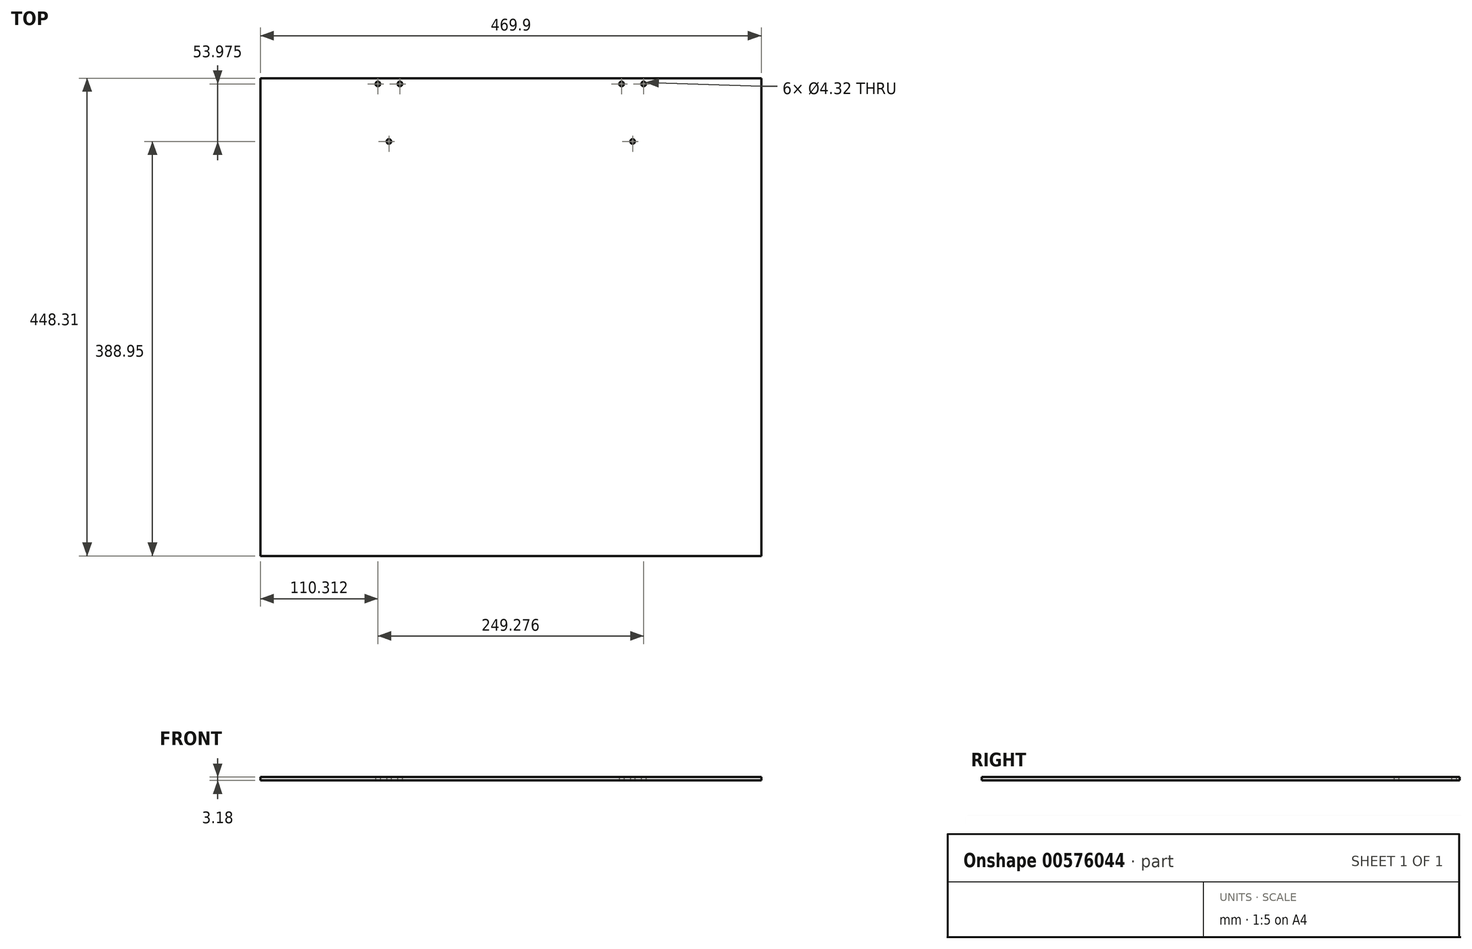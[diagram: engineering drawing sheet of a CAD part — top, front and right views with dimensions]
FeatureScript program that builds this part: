
annotation { "Feature Type Name" : "Feature", "Feature Type Description" : "" }
export const myFeature = defineFeature(function(context is Context, id is Id, definition is map)
    precondition{}
    {
        {
            var Q0;
            Q0=qCreatedBy(makeId("Top.planeOp"),FACE);
            var sketch = newSketch(context, id + "F0", { "sketchPlane" : qUnion([Q0])});
            skLineSegment(sketch, "E0.bottom", {"start": v(234.95, -234.95) * mm, "end": v(-234.95, -234.95) * mm});
            skLineSegment(sketch, "E0.top", {"start": v(234.95, 234.95) * mm, "end": v(-234.95, 234.95) * mm});
            skLineSegment(sketch, "E0.left", {"start": v(234.95, -234.95) * mm, "end": v(234.95, 234.95) * mm});
            skLineSegment(sketch, "E0.right", {"start": v(-234.95, -234.95) * mm, "end": v(-234.95, 234.95) * mm});
            skPoint(sketch, "E0.middle", {"position": v(0, 0) * mm});
            skSolve(sketch);
        }
        {
            var Q0;
            Q0=qSketchRegion(id+"F0",true);
            extrude(context, id + "F1", {"entities" : qUnion([Q0]), "depth" : 3.17 * mm, "offsetDistance" : 25.4 * mm});
        }
        {
            var Q0;
            Q0=makeQuery(id+"F1.opExtrude","CAP_FACE",FACE,{"disambiguationData":[OSD([sQuery(id+"F0.wireOp",EDGE,"E0.bottom"),sQuery(id+"F0.wireOp",EDGE,"E0.top"),sQuery(id+"F0.wireOp",EDGE,"E0.left"),sQuery(id+"F0.wireOp",EDGE,"E0.right")])],"isStart":true});
            var sketch = newSketch(context, id + "F2", { "sketchPlane" : qUnion([Q0])});
            skLineSegment(sketch, "E1", {"start": v(234.95, -234.95) * mm, "end": v(158.75, -234.95) * mm});
            skLineSegment(sketch, "E2", {"start": v(158.75, -234.95) * mm, "end": v(114.3, -234.95) * mm});
            skLineSegment(sketch, "E3", {"start": v(114.3, -234.95) * mm, "end": v(114.3, -214.33) * mm});
            skLineSegment(sketch, "E4", {"start": v(114.3, -214.33) * mm, "end": v(124.64, -214.33) * mm});
            skLineSegment(sketch, "E5", {"start": v(114.3, -234.95) * mm, "end": v(114.3, -160.35) * mm});
            skLineSegment(sketch, "E6.MirrorCS", {"start": v(114.3, -214.33) * mm, "end": v(103.96, -214.33) * mm});
            skLineSegment(sketch, "E7", {"start": v(0, -234.95) * mm, "end": v(0, -342.5) * mm});
            skLineSegment(sketch, "E8.MirrorCS", {"start": v(-158.75, -234.95) * mm, "end": v(-114.3, -234.95) * mm});
            skLineSegment(sketch, "E9.MirrorCS", {"start": v(-114.3, -214.33) * mm, "end": v(-124.64, -214.33) * mm});
            skLineSegment(sketch, "E10.MirrorCS", {"start": v(-114.3, -214.33) * mm, "end": v(-103.96, -214.33) * mm});
            skLineSegment(sketch, "E11.MirrorCS", {"start": v(-234.95, -234.95) * mm, "end": v(-158.75, -234.95) * mm});
            skLineSegment(sketch, "E12.MirrorCS", {"start": v(-114.3, -234.95) * mm, "end": v(-114.3, -214.33) * mm});
            skLineSegment(sketch, "E13.MirrorCS", {"start": v(-114.3, -234.95) * mm, "end": v(-114.3, -160.35) * mm});
            skSolve(sketch);
        }
        {
            var Q0;
            Q0=sQuery(id+"F2.wireOp",VERTEX,"E4.end");
            var Q1;
            Q1=sQuery(id+"F2.wireOp",VERTEX,"E6.MirrorCS.end");
            var Q2;
            Q2=sQuery(id+"F2.wireOp",VERTEX,"E5.end");
            var Q3;
            Q3=sQuery(id+"F2.wireOp",VERTEX,"E13.MirrorCS.end");
            var Q4;
            Q4=sQuery(id+"F2.wireOp",VERTEX,"E10.MirrorCS.end");
            var Q5;
            Q5=sQuery(id+"F2.wireOp",VERTEX,"E9.MirrorCS.end");
            var Q6;
            Q6=makeQuery(id+"F1.opExtrude","SWEPT_BODY",BODY,{"disambiguationData":[OSD([sQuery(id+"F0.wireOp",EDGE,"E0.bottom"),sQuery(id+"F0.wireOp",EDGE,"E0.top"),sQuery(id+"F0.wireOp",EDGE,"E0.left"),sQuery(id+"F0.wireOp",EDGE,"E0.right")])]});
            hole(context, id + "F3", {"style" : HoleStyle.SIMPLE, "endStyle" : HoleEndStyle.THROUGH, "standardTappedOrClearance" : lookupTablePath({ "standard" : "ANSI", "fit" : "Close", "size" : "#8", "type" : "Clearance" }), "standardBlindInLast" : lookupTablePath({ "fit" : "Close", "standard" : "ANSI", "size" : "#8", "type" : "Clearance" }), "holeDiameter" : 4.32 * mm, "isTappedThrough" : true, "tappedDepth" : 12.7 * mm, "tapClearance" : 3, "locations" : qUnion([Q0, Q1, Q2, Q3, Q4, Q5]), "scope" : qUnion([Q6])});
        }
        {
            var Q0;
            Q0=makeQuery(id+"F1.opExtrude","SWEPT_FACE",FACE,{"disambiguationData":[OSD([sQuery(id+"F0.wireOp",EDGE,"E0.top")])]});
            extrude(context, id + "F4", {"entities" : qUnion([Q0]), "operationType" : NewBodyOperationType.REMOVE, "oppositeDirection" : true, "depth" : 15.24 * mm, "offsetDistance" : 25.4 * mm});
        }
        {
            var Q0;
            Q0=makeQuery(id+"F1.opExtrude","SWEPT_FACE",FACE,{"disambiguationData":[OSD([sQuery(id+"F0.wireOp",EDGE,"E0.bottom")])]});
            extrude(context, id + "F5", {"entities" : qUnion([Q0]), "operationType" : NewBodyOperationType.REMOVE, "oppositeDirection" : true, "depth" : 6.35 * mm, "offsetDistance" : 25.4 * mm});
        }
    });
